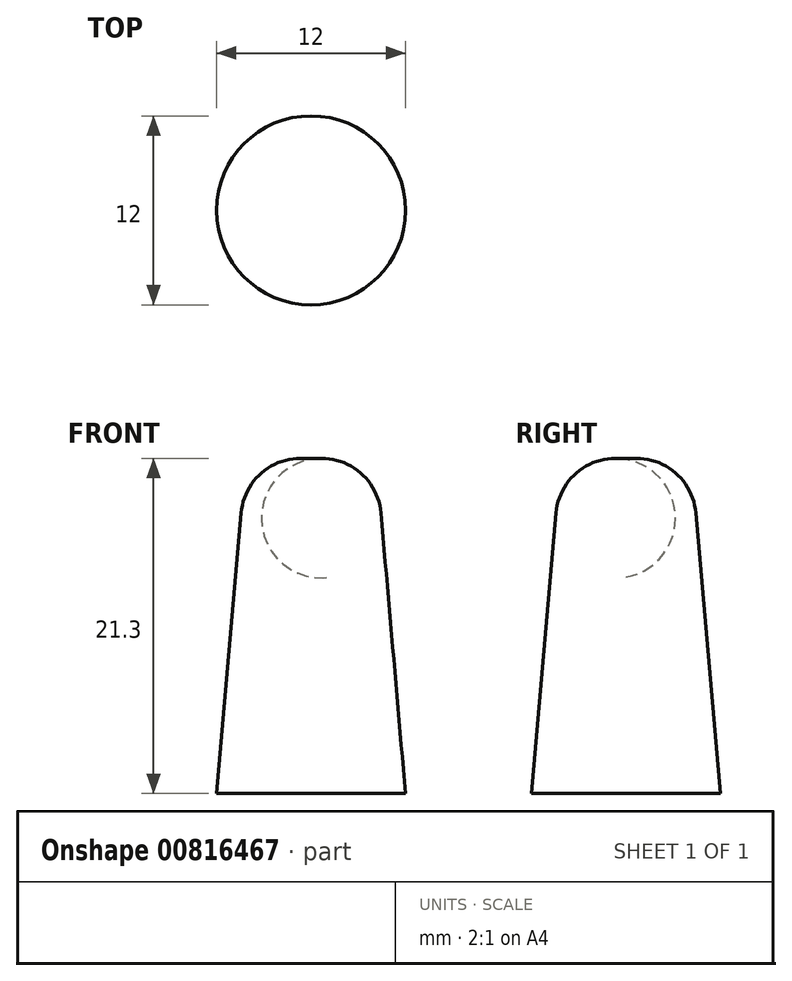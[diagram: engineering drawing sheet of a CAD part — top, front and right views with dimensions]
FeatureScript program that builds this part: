
annotation { "Feature Type Name" : "Feature", "Feature Type Description" : "" }
export const myFeature = defineFeature(function(context is Context, id is Id, definition is map)
    precondition{}
    {
        {
            var Q0;
            Q0=qCreatedBy(makeId("Right.planeOp"),FACE);
            var sketch = newSketch(context, id + "F0", { "sketchPlane" : qUnion([Q0])});
            skLineSegment(sketch, "E0", {"start": v(0, 21.24) * mm, "end": v(0, 0) * mm});
            skLineSegment(sketch, "E1", {"start": v(0, 0) * mm, "end": v(6, 0) * mm});
            skLineSegment(sketch, "E2", {"start": v(6, 0) * mm, "end": v(4.44, 17.83) * mm});
            skArc(sketch, "E3", {"start": v(4.44, 17.83) * mm, "mid": v(2.97, 20.51) * mm, "end": v(0, 21.24) * mm});
            skSolve(sketch);
        }
        {
            var Q0;
            Q0=makeQuery(id+"F0.imprint","IMPRINT",FACE,{"disambiguationData":[TD([[makeQuery(id+"F0.imprint","IMPRINT",EDGE,{"derivedFrom":sQuery(id+"F0.wireOp",EDGE,"E0")}),1.0]])]});
            var Q1;
            Q1=sQuery(id+"F0.wireOp",EDGE,"E0");
            revolve(context, id + "F1", {"surfaceOperationType" : NewSurfaceOperationType.NEW, "entities" : qUnion([Q0]), "axis" : qUnion([Q1]), "revolveType" : RevolveType.FULL});
        }
    });
